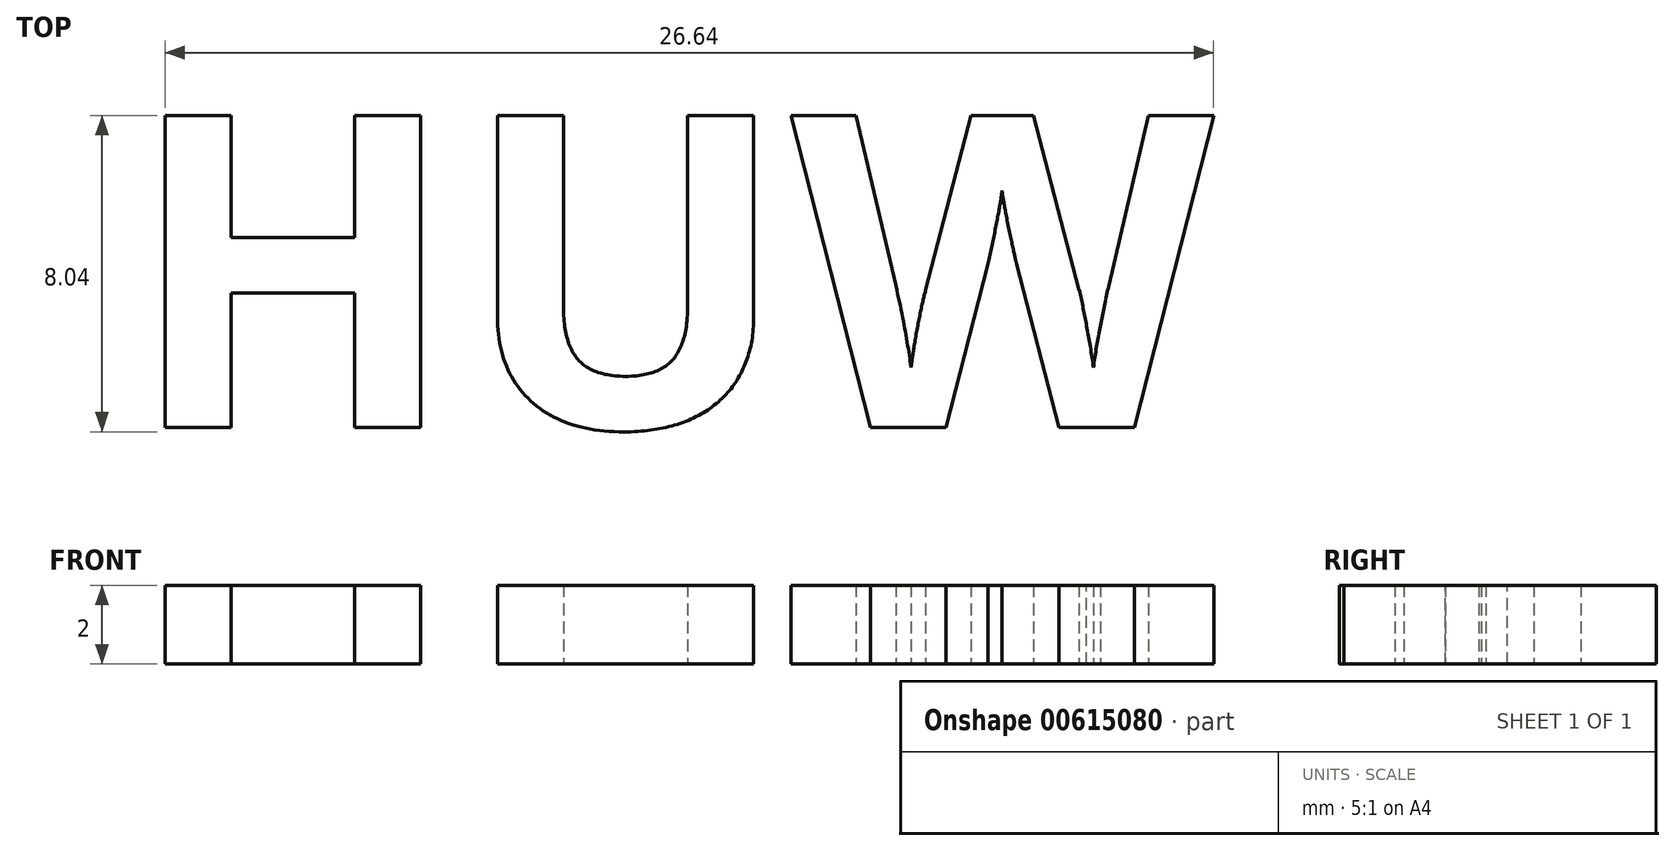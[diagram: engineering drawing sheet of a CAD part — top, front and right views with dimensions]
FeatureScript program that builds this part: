
annotation { "Feature Type Name" : "Feature", "Feature Type Description" : "" }
export const myFeature = defineFeature(function(context is Context, id is Id, definition is map)
    precondition{}
    {
        {
            var Q0;
            Q0=qCreatedBy(makeId("Top.planeOp"),FACE);
            var sketch = newSketch(context, id + "F0", { "sketchPlane" : qUnion([Q0])});
            skText(sketch, "E0", { "text": "HUW", "fontName": "OpenSans-Bold.ttf"});
            const initialGuessF0  = {"E0": [-0.08987, -0.0562, 1, 0, 0.008]};
            skSetInitialGuess(sketch, initialGuessF0);
            skSolve(sketch);
        }
        {
            var Q0;
            Q0 = qSketchRegion(id + "F0", true);
            extrude(context, id + "F1", {"entities" : qUnion([Q0]), "depth" : 2 * mm, "offsetDistance" : 25 * mm});
        }
    });
